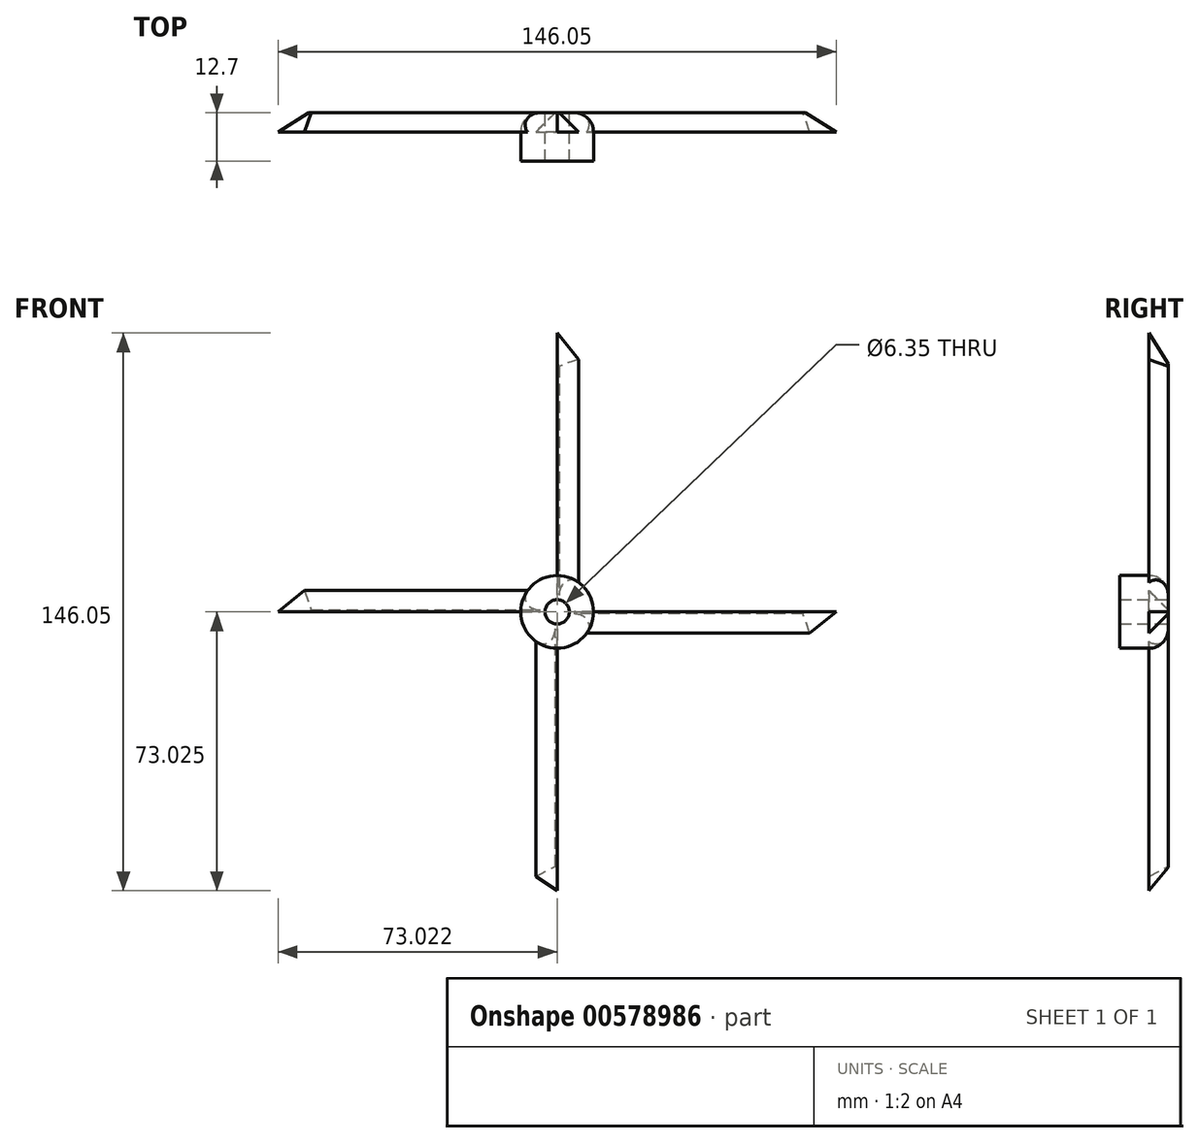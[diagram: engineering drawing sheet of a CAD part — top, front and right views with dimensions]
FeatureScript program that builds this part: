
annotation { "Feature Type Name" : "Feature", "Feature Type Description" : "" }
export const myFeature = defineFeature(function(context is Context, id is Id, definition is map)
    precondition{}
    {
        {
            var Q0;
            Q0=qCreatedBy(makeId("Front.planeOp"),FACE);
            var sketch = newSketch(context, id + "F0", { "sketchPlane" : qUnion([Q0])});
            skCircle(sketch, "E0", {"center": v(8.12, 14.12) * mm, "radius": 3.18 * mm});
            skCircle(sketch, "E1", {"center": v(8.12, 14.12) * mm, "radius": 9.53 * mm});
            skLineSegment(sketch, "E2", {"start": v(8.12, 23.65) * mm, "end": v(8.12, 87.15) * mm});
            skLineSegment(sketch, "E3", {"start": v(8.12, 4.6) * mm, "end": v(8.12, -58.9) * mm});
            skLineSegment(sketch, "E4", {"start": v(-1.4, 14.12) * mm, "end": v(-64.9, 14.12) * mm});
            skLineSegment(sketch, "E5", {"start": v(-64.9, 14.12) * mm, "end": v(-58.01, 19.71) * mm});
            skLineSegment(sketch, "E6", {"start": v(-58.01, 19.71) * mm, "end": v(0.4, 19.71) * mm});
            skLineSegment(sketch, "E7", {"start": v(8.12, 87.15) * mm, "end": v(13.7, 80.26) * mm});
            skLineSegment(sketch, "E8", {"start": v(13.7, 80.26) * mm, "end": v(13.7, 21.84) * mm});
            skLineSegment(sketch, "E9", {"start": v(8.12, -58.9) * mm, "end": v(2.53, -55.22) * mm});
            skLineSegment(sketch, "E10", {"start": v(2.53, -55.22) * mm, "end": v(2.53, 6.41) * mm});
            skLineSegment(sketch, "E11", {"start": v(17.65, 14.12) * mm, "end": v(81.15, 14.12) * mm});
            skLineSegment(sketch, "E12", {"start": v(81.15, 14.12) * mm, "end": v(74.26, 8.54) * mm});
            skLineSegment(sketch, "E13", {"start": v(74.26, 8.54) * mm, "end": v(15.84, 8.54) * mm});
            skSolve(sketch);
        }
        {
            var Q0;
            Q0=makeQuery(id+"F0.imprint","IMPRINT",FACE,{"disambiguationData":[TD([[makeQuery(id+"F0.imprint","IMPRINT",EDGE,{"derivedFrom":sQuery(id+"F0.wireOp",EDGE,"E0")}),-1.0]])]});
            extrude(context, id + "F1", {"entities" : qUnion([Q0]), "depth" : 12.7 * mm, "offsetDistance" : 25.4 * mm});
        }
        {
            var Q0;
            {var subQ0=sQuery(id+"F0.wireOp",EDGE,"E2");Q0=makeQuery(id+"F0.imprint","IMPRINT",FACE,{"disambiguationData":[TD([[makeQuery(id+"F0.imprint","IMPRINT",EDGE,{"derivedFrom":subQ0}),-1.0]])]});}
            var Q1;
            {var subQ0=sQuery(id+"F0.wireOp",EDGE,"E11");Q1=makeQuery(id+"F0.imprint","IMPRINT",FACE,{"disambiguationData":[TD([[makeQuery(id+"F0.imprint","IMPRINT",EDGE,{"derivedFrom":subQ0}),-1.0]])]});}
            var Q2;
            {var subQ0=sQuery(id+"F0.wireOp",EDGE,"E4");Q2=makeQuery(id+"F0.imprint","IMPRINT",FACE,{"disambiguationData":[TD([[makeQuery(id+"F0.imprint","IMPRINT",EDGE,{"derivedFrom":subQ0}),-1.0]])]});}
            var Q3;
            {var subQ0=sQuery(id+"F0.wireOp",EDGE,"E3");Q3=makeQuery(id+"F0.imprint","IMPRINT",FACE,{"disambiguationData":[TD([[makeQuery(id+"F0.imprint","IMPRINT",EDGE,{"derivedFrom":subQ0}),-1.0]])]});}
            extrude(context, id + "F2", {"entities" : qUnion([Q0, Q1, Q2, Q3]), "operationType" : NewBodyOperationType.ADD, "depth" : 5.08 * mm, "offsetDistance" : 25.4 * mm});
        }
        {
            var Q0;
            Q0=makeQuery(id+"F2.opExtrude","CAP_EDGE",EDGE,{"disambiguationData":[OSD([sQuery(id+"F0.wireOp",EDGE,"E12")])],"isStart":true});
            var Q1;
            Q1=makeQuery(id+"F2.opExtrude","CAP_EDGE",EDGE,{"disambiguationData":[OSD([sQuery(id+"F0.wireOp",EDGE,"E13")])],"isStart":true});
            var Q2;
            Q2=makeQuery(id+"F2.opExtrude","CAP_EDGE",EDGE,{"disambiguationData":[OSD([sQuery(id+"F0.wireOp",EDGE,"E8")])],"isStart":true});
            var Q3;
            Q3=makeQuery(id+"F2.opExtrude","CAP_EDGE",EDGE,{"disambiguationData":[OSD([sQuery(id+"F0.wireOp",EDGE,"E7")])],"isStart":true});
            var Q4;
            Q4=makeQuery(id+"F2.opExtrude","CAP_EDGE",EDGE,{"disambiguationData":[OSD([sQuery(id+"F0.wireOp",EDGE,"E10")])],"isStart":true});
            var Q5;
            Q5=makeQuery(id+"F2.opExtrude","CAP_EDGE",EDGE,{"disambiguationData":[OSD([sQuery(id+"F0.wireOp",EDGE,"E9")])],"isStart":true});
            var Q6;
            Q6=makeQuery(id+"F2.opExtrude","CAP_EDGE",EDGE,{"disambiguationData":[OSD([sQuery(id+"F0.wireOp",EDGE,"E6")])],"isStart":true});
            var Q7;
            Q7=makeQuery(id+"F2.opExtrude","CAP_EDGE",EDGE,{"disambiguationData":[OSD([sQuery(id+"F0.wireOp",EDGE,"E5")])],"isStart":true});
            chamfer(context, id + "F3", {"entities" : qUnion([Q0, Q1, Q2, Q3, Q4, Q5, Q6, Q7]), "width" : 5.08 * mm, "tangentPropagation" : true});
        }
        {
            var Q0;
            {var subQ0=sQuery(id+"F0.wireOp",EDGE,"E1");var subQ1=sQuery(id+"F0.wireOp",EDGE,"E8");Q0=makeQuery(id+"F2.boolean.opBoolean","SPLIT",EDGE,{"disambiguationData":[TD([makeQuery(id+"F2.opExtrude","SWEPT_FACE",FACE,{"disambiguationData":[OSD([subQ1])]})])],"derivedFrom":makeQuery(id+"F1.opExtrude","CAP_EDGE",EDGE,{"disambiguationData":[OSD([subQ0])],"isStart":true})});}
            var Q1;
            {var subQ0=sQuery(id+"F0.wireOp",EDGE,"E1");var subQ2=sQuery(id+"F0.wireOp",EDGE,"E3");Q1=makeQuery(id+"F2.boolean.opBoolean","SPLIT",EDGE,{"disambiguationData":[TD([makeQuery(id+"F2.opExtrude","SWEPT_FACE",FACE,{"disambiguationData":[OSD([subQ2])]})])],"derivedFrom":makeQuery(id+"F1.opExtrude","CAP_EDGE",EDGE,{"disambiguationData":[OSD([subQ0])],"isStart":true})});}
            var Q2;
            {var subQ1=sQuery(id+"F0.wireOp",EDGE,"E1");var subQ2=sQuery(id+"F0.wireOp",EDGE,"E2");Q2=makeQuery(id+"F2.boolean.opBoolean","SPLIT",EDGE,{"disambiguationData":[TD([makeQuery(id+"F2.opExtrude","SWEPT_FACE",FACE,{"disambiguationData":[OSD([subQ2])]})])],"derivedFrom":makeQuery(id+"F1.opExtrude","CAP_EDGE",EDGE,{"disambiguationData":[OSD([subQ1])],"isStart":true})});}
            var Q3;
            {var subQ0=sQuery(id+"F0.wireOp",EDGE,"E4");var subQ1=sQuery(id+"F0.wireOp",EDGE,"E1");Q3=makeQuery(id+"F2.boolean.opBoolean","SPLIT",EDGE,{"disambiguationData":[TD([makeQuery(id+"F2.opExtrude","SWEPT_FACE",FACE,{"disambiguationData":[OSD([subQ0])]})])],"derivedFrom":makeQuery(id+"F1.opExtrude","CAP_EDGE",EDGE,{"disambiguationData":[OSD([subQ1])],"isStart":true})});}
            fillet(context, id + "F4", {"entities" : qUnion([Q0, Q1, Q2, Q3]), "radius" : 5.08 * mm, "tangentPropagation" : true, "allowEdgeOverflow" : false});
        }
    });
